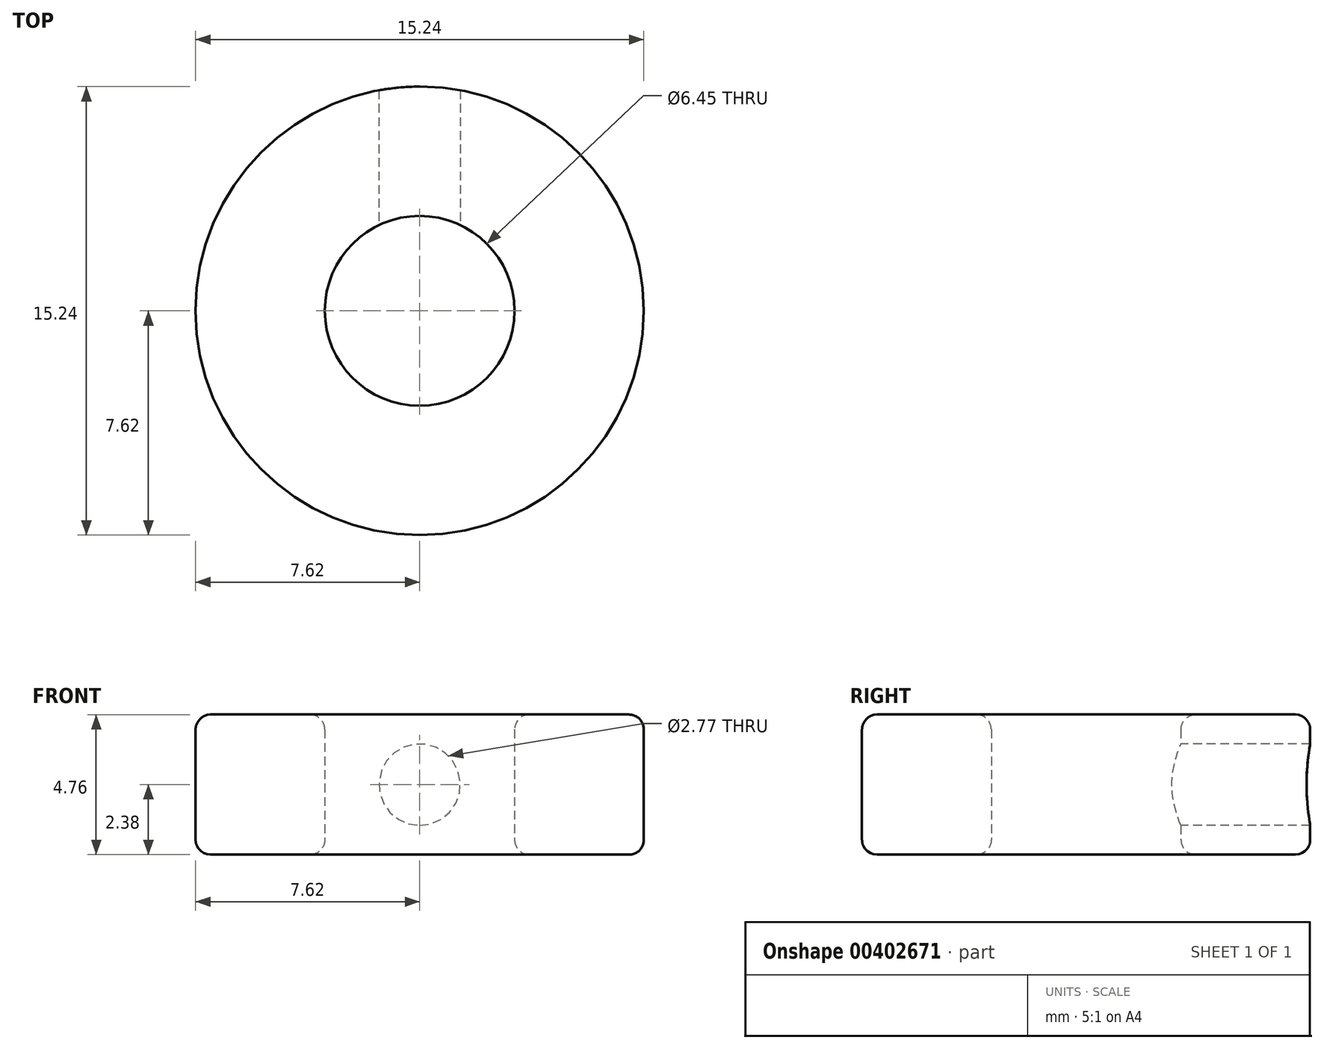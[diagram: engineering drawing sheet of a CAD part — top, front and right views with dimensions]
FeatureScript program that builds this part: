
annotation { "Feature Type Name" : "Feature", "Feature Type Description" : "" }
export const myFeature = defineFeature(function(context is Context, id is Id, definition is map)
    precondition{}
    {
        {
            var Q0;
            Q0=qCreatedBy(makeId("Top.planeOp"),FACE);
            var sketch = newSketch(context, id + "F0", { "sketchPlane" : qUnion([Q0])});
            skCircle(sketch, "E0", {"center": v(0, 0) * mm, "radius": 7.62 * mm});
            skCircle(sketch, "E1", {"center": v(0, 0) * mm, "radius": 3.23 * mm});
            skSolve(sketch);
        }
        {
            var Q0;
            Q0 = qSketchRegion(id + "F0", true);
            extrude(context, id + "F1", {"entities" : qUnion([Q0]), "endBound" : BoundingType.SYMMETRIC, "depth" : 4.76 * mm});
        }
        {
            var Q0;
            Q0=qCreatedBy(makeId("Front.planeOp"),FACE);
            var sketch = newSketch(context, id + "F2", { "sketchPlane" : qUnion([Q0])});
            skCircle(sketch, "E2", {"center": v(0, 0) * mm, "radius": 1.38 * mm});
            skSolve(sketch);
        }
        {
            var Q0;
            Q0 = qSketchRegion(id + "F2", true);
            extrude(context, id + "F3", {"entities" : qUnion([Q0]), "operationType" : NewBodyOperationType.REMOVE, "oppositeDirection" : true, "depth" : 7.62 * mm});
        }
        {
            var Q0;
            Q0=makeQuery(id+"F1.opExtrude","CAP_EDGE",EDGE,{"disambiguationData":[OSD([sQuery(id+"F0.wireOp",EDGE,"E0")])],"isStart":false});
            var Q1;
            Q1=makeQuery(id+"F1.opExtrude","CAP_EDGE",EDGE,{"disambiguationData":[OSD([sQuery(id+"F0.wireOp",EDGE,"E0")])],"isStart":true});
            var Q2;
            Q2=makeQuery(id+"F1.opExtrude","CAP_EDGE",EDGE,{"disambiguationData":[OSD([sQuery(id+"F0.wireOp",EDGE,"E1")])],"isStart":true});
            var Q3;
            Q3=makeQuery(id+"F1.opExtrude","CAP_EDGE",EDGE,{"disambiguationData":[OSD([sQuery(id+"F0.wireOp",EDGE,"E1")])],"isStart":false});
            fillet(context, id + "F4", {"entities" : qUnion([Q0, Q1, Q2, Q3]), "radius" : 0.5 * mm, "tangentPropagation" : true, "allowEdgeOverflow" : false});
        }
    });
